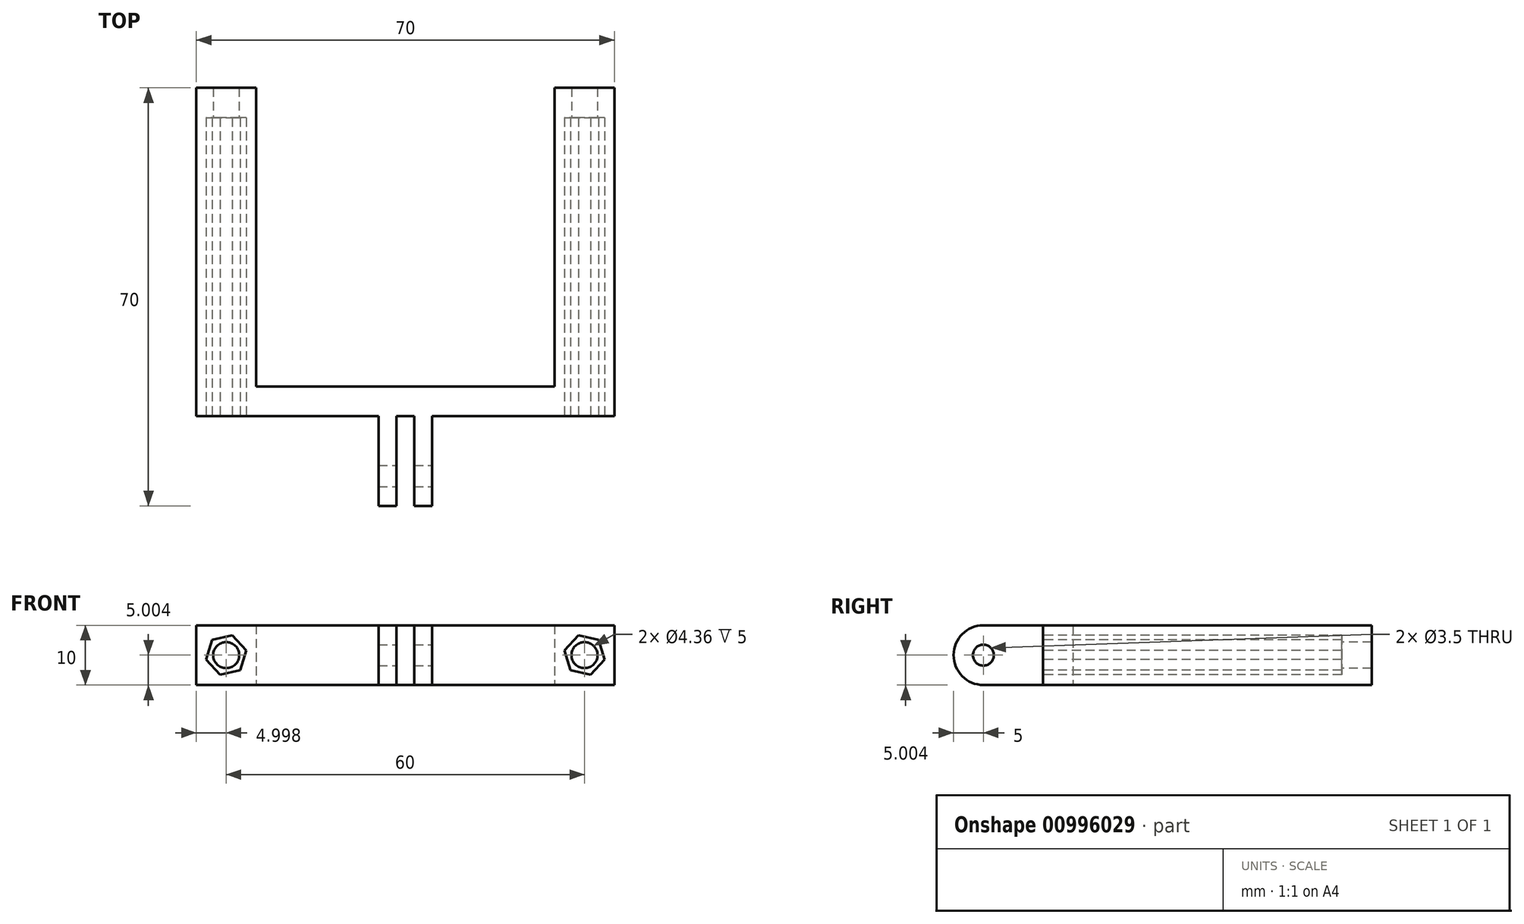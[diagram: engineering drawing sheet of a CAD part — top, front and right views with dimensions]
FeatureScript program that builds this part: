
annotation { "Feature Type Name" : "Feature", "Feature Type Description" : "" }
export const myFeature = defineFeature(function(context is Context, id is Id, definition is map)
    precondition{}
    {
        {
            var Q0;
            Q0=qCreatedBy(makeId("Front.planeOp"),FACE);
            var sketch = newSketch(context, id + "F0", { "sketchPlane" : qUnion([Q0])});
            skLineSegment(sketch, "E0.bottom", {"start": v(-29.53, -0.3) * mm, "end": v(-19.53, -0.3) * mm});
            skLineSegment(sketch, "E0.top", {"start": v(-29.53, -10.3) * mm, "end": v(-19.53, -10.3) * mm});
            skLineSegment(sketch, "E0.left", {"start": v(-29.53, -0.3) * mm, "end": v(-29.53, -10.3) * mm});
            skLineSegment(sketch, "E0.right", {"start": v(-19.53, -0.3) * mm, "end": v(-19.53, -10.3) * mm});
            skCircle(sketch, "E1", {"center": v(-24.53, -5.3) * mm, "radius": 2.18 * mm});
            skPoint(sketch, "E2", {"position": v(-24.53, -10.3) * mm});
            skPoint(sketch, "E3", {"position": v(-19.53, -5.3) * mm});
            skSolve(sketch);
        }
        {
            var Q0;
            Q0=makeQuery(id+"F0.imprint","IMPRINT",FACE,{"disambiguationData":[TD([[makeQuery(id+"F0.imprint","IMPRINT",EDGE,{"derivedFrom":sQuery(id+"F0.wireOp",EDGE,"rqn8Xpzs-wxr6-XT8o-bE4w-pqP2pNNWYZRO.bottom")}),-1.0]])]});
            var Q1;
            Q1=makeQuery(id+"F0.imprint","IMPRINT",FACE,{"disambiguationData":[TD([[makeQuery(id+"F0.imprint","IMPRINT",EDGE,{"derivedFrom":sQuery(id+"F0.wireOp",EDGE,"E0.bottom")}),-1.0]])]});
            extrude(context, id + "F1", {"entities" : qUnion([Q0, Q1]), "oppositeDirection" : true, "depth" : 50 * mm, "offsetDistance" : 25 * mm});
        }
        {
            var Q0;
            Q0=makeQuery(id+"F1.opExtrude","CAP_FACE",FACE,{"disambiguationData":[OSD([sQuery(id+"F0.wireOp",EDGE,"E0.bottom"),sQuery(id+"F0.wireOp",EDGE,"E0.top"),sQuery(id+"F0.wireOp",EDGE,"E0.left"),sQuery(id+"F0.wireOp",EDGE,"E0.right"),sQuery(id+"F0.wireOp",EDGE,"E1")])],"isStart":true});
            var sketch = newSketch(context, id + "F2", { "sketchPlane" : qUnion([Q0])});
            skLineSegment(sketch, "E4.0", {"start": v(30.47, -10.3) * mm, "end": v(40.47, -10.3) * mm});
            skLineSegment(sketch, "E5.bottom", {"start": v(-29.53, -0.3) * mm, "end": v(40.47, -0.3) * mm});
            skLineSegment(sketch, "E5.top", {"start": v(-29.53, -10.3) * mm, "end": v(40.47, -10.3) * mm});
            skLineSegment(sketch, "E5.left", {"start": v(-29.53, -0.3) * mm, "end": v(-29.53, -10.3) * mm});
            skLineSegment(sketch, "E5.right", {"start": v(40.47, -0.3) * mm, "end": v(40.47, -10.3) * mm});
            skCircle(sketch, "E6.cCircle", {"center": v(-24.53, -5.3) * mm, "radius": 3 * mm, "construction": true});
            skLineSegment(sketch, "E6.0", {"start": v(-21.15, -4.53) * mm, "end": v(-22.18, -7.84) * mm});
            skLineSegment(sketch, "E6.1", {"start": v(-22.18, -7.84) * mm, "end": v(-25.55, -8.62) * mm});
            skLineSegment(sketch, "E6.2", {"start": v(-25.55, -8.62) * mm, "end": v(-27.9, -6.08) * mm});
            skLineSegment(sketch, "E6.3", {"start": v(-27.9, -6.08) * mm, "end": v(-26.89, -2.77) * mm});
            skLineSegment(sketch, "E6.4", {"start": v(-26.89, -2.77) * mm, "end": v(-23.51, -2) * mm});
            skLineSegment(sketch, "E6.5", {"start": v(-23.51, -2) * mm, "end": v(-21.15, -4.53) * mm});
            skPoint(sketch, "E6.0.midPoint", {"position": v(-21.66, -6.19) * mm});
            skCircle(sketch, "E7.0", {"center": v(35.47, -5.3) * mm, "radius": 1.75 * mm});
            skCircle(sketch, "E8.cCircle", {"center": v(35.47, -5.3) * mm, "radius": 3 * mm, "construction": true});
            skLineSegment(sketch, "E8.0", {"start": v(38.92, -5.55) * mm, "end": v(36.99, -8.42) * mm});
            skLineSegment(sketch, "E8.1", {"start": v(36.99, -8.42) * mm, "end": v(33.53, -8.18) * mm});
            skLineSegment(sketch, "E8.2", {"start": v(33.53, -8.18) * mm, "end": v(32.01, -5.06) * mm});
            skLineSegment(sketch, "E8.3", {"start": v(32.01, -5.06) * mm, "end": v(33.95, -2.2) * mm});
            skLineSegment(sketch, "E8.4", {"start": v(33.95, -2.2) * mm, "end": v(37.4, -2.43) * mm});
            skLineSegment(sketch, "E8.5", {"start": v(37.4, -2.43) * mm, "end": v(38.92, -5.55) * mm});
            skPoint(sketch, "E8.0.midPoint", {"position": v(37.95, -6.98) * mm});
            skSolve(sketch);
        }
        {
            var Q0;
            Q0=makeQuery(id+"F2.imprint","IMPRINT",FACE,{"disambiguationData":[TD([[makeQuery(id+"F2.imprint","IMPRINT",EDGE,{"derivedFrom":sQuery(id+"F2.wireOp",EDGE,"E6.0")}),-1.0]])]});
            var Q1;
            Q1=makeQuery(id+"F2.imprint","IMPRINT",FACE,{"disambiguationData":[TD([[makeQuery(id+"F2.imprint","IMPRINT",EDGE,{"derivedFrom":sQuery(id+"F2.wireOp",EDGE,"E7.0")}),-1.0]])]});
            extrude(context, id + "F3", {"entities" : qUnion([Q0, Q1]), "operationType" : NewBodyOperationType.REMOVE, "oppositeDirection" : true, "depth" : 45 * mm, "offsetDistance" : 25 * mm});
        }
        {
            var Q0;
            Q0=makeQuery(id+"F1.opExtrude","CAP_FACE",FACE,{"disambiguationData":[OSD([sQuery(id+"F0.wireOp",EDGE,"E0.bottom"),sQuery(id+"F0.wireOp",EDGE,"E0.top"),sQuery(id+"F0.wireOp",EDGE,"E0.left"),sQuery(id+"F0.wireOp",EDGE,"E0.right"),sQuery(id+"F0.wireOp",EDGE,"E1")])],"isStart":true});
            var sketch = newSketch(context, id + "F4", { "sketchPlane" : qUnion([Q0])});
            skLineSegment(sketch, "E9.bottom", {"start": v(-29.53, -0.3) * mm, "end": v(5.47, -0.3) * mm});
            skLineSegment(sketch, "E9.top", {"start": v(-29.53, -10.3) * mm, "end": v(5.47, -10.3) * mm});
            skLineSegment(sketch, "E9.left", {"start": v(-29.53, -0.3) * mm, "end": v(-29.53, -10.3) * mm});
            skLineSegment(sketch, "E9.right", {"start": v(5.47, -0.3) * mm, "end": v(5.47, -10.3) * mm});
            skLineSegment(sketch, "E10.0", {"start": v(-25.55, -8.62) * mm, "end": v(-27.9, -6.08) * mm});
            skLineSegment(sketch, "E11.0", {"start": v(-27.9, -6.08) * mm, "end": v(-26.89, -2.77) * mm});
            skPoint(sketch, "E12.0", {"position": v(-26.89, -2.77) * mm});
            skLineSegment(sketch, "E13.0", {"start": v(-26.89, -2.77) * mm, "end": v(-23.51, -2) * mm});
            skPoint(sketch, "E14.0", {"position": v(-22.33, -3.27) * mm});
            skLineSegment(sketch, "E15.0", {"start": v(-23.51, -2) * mm, "end": v(-21.15, -4.53) * mm});
            skLineSegment(sketch, "E16.0", {"start": v(-21.15, -4.53) * mm, "end": v(-22.18, -7.84) * mm});
            skLineSegment(sketch, "E17.0", {"start": v(-22.18, -7.84) * mm, "end": v(-25.55, -8.62) * mm});
            skSolve(sketch);
        }
        {
            var Q0;
            Q0 = qSketchRegion(id + "F4", true);
            extrude(context, id + "F5", {"entities" : qUnion([Q0]), "operationType" : NewBodyOperationType.ADD, "depth" : 5 * mm, "offsetDistance" : 25 * mm});
        }
        {
            var Q0;
            Q0=makeQuery(id+"F1.opExtrude","SWEPT_BODY",BODY,{"disambiguationData":[OSD([sQuery(id+"F0.wireOp",EDGE,"E0.bottom"),sQuery(id+"F0.wireOp",EDGE,"E0.top"),sQuery(id+"F0.wireOp",EDGE,"E0.left"),sQuery(id+"F0.wireOp",EDGE,"E0.right"),sQuery(id+"F0.wireOp",EDGE,"E1")])]});
            var Q1;
            Q1=makeQuery(id+"F5.opExtrude","SWEPT_FACE",FACE,{"disambiguationData":[OSD([sQuery(id+"F4.wireOp",EDGE,"E9.right")])]});
            mirror(context, id + "F6", {"operationType" : NewBodyOperationType.ADD, "entities" : qUnion([Q0]), "mirrorPlane" : qUnion([Q1])});
        }
        {
            var Q0;
            {var subQ0=makeQuery(id+"F5.opExtrude","CAP_FACE",FACE,{"disambiguationData":[OSD([sQuery(id+"F4.wireOp",EDGE,"E9.bottom"),sQuery(id+"F4.wireOp",EDGE,"E9.top"),sQuery(id+"F4.wireOp",EDGE,"E9.left"),sQuery(id+"F4.wireOp",EDGE,"E9.right"),sQuery(id+"F4.wireOp",EDGE,"E10.0"),sQuery(id+"F4.wireOp",EDGE,"E11.0"),sQuery(id+"F4.wireOp",EDGE,"E13.0"),sQuery(id+"F4.wireOp",EDGE,"E15.0"),sQuery(id+"F4.wireOp",EDGE,"E16.0"),sQuery(id+"F4.wireOp",EDGE,"E17.0")])],"isStart":false});Q0=makeQuery(id+"F6.boolean.opBoolean","MERGE",FACE,{"derivedFrom":[subQ0,makeQuery(id+"F6.opPattern","COPY",FACE,{"derivedFrom":subQ0,"instanceName":"1"})]});}
            var sketch = newSketch(context, id + "F7", { "sketchPlane" : qUnion([Q0])});
            skLineSegment(sketch, "E18.0", {"start": v(-29.53, -0.3) * mm, "end": v(40.47, -0.3) * mm});
            skLineSegment(sketch, "E19.0", {"start": v(-29.53, -10.3) * mm, "end": v(40.47, -10.3) * mm});
            skPoint(sketch, "E20", {"position": v(5.47, -0.3) * mm});
            skPoint(sketch, "E21", {"position": v(5.47, -10.3) * mm});
            skLineSegment(sketch, "E22", {"start": v(5.47, -0.3) * mm, "end": v(5.47, -10.3) * mm, "construction": true});
            skLineSegment(sketch, "E23.bottom", {"start": v(3.97, -0.3) * mm, "end": v(0.97, -0.3) * mm});
            skLineSegment(sketch, "E23.top", {"start": v(3.97, -10.3) * mm, "end": v(0.97, -10.3) * mm});
            skLineSegment(sketch, "E23.left", {"start": v(3.97, -0.3) * mm, "end": v(3.97, -10.3) * mm});
            skLineSegment(sketch, "E23.right", {"start": v(0.97, -0.3) * mm, "end": v(0.97, -10.3) * mm});
            skLineSegment(sketch, "E24.bottom", {"start": v(6.97, -0.3) * mm, "end": v(9.97, -0.3) * mm});
            skLineSegment(sketch, "E24.top", {"start": v(6.97, -10.3) * mm, "end": v(9.97, -10.3) * mm});
            skLineSegment(sketch, "E24.left", {"start": v(6.97, -0.3) * mm, "end": v(6.97, -10.3) * mm});
            skLineSegment(sketch, "E24.right", {"start": v(9.97, -0.3) * mm, "end": v(9.97, -10.3) * mm});
            skSolve(sketch);
        }
        {
            var Q0;
            {var subQ0=sQuery(id+"F7.wireOp",EDGE,"E24.left");Q0=makeQuery(id+"F7.imprint","IMPRINT",FACE,{"disambiguationData":[TD([[makeQuery(id+"F7.imprint","IMPRINT",EDGE,{"derivedFrom":subQ0}),1.0]])]});}
            var Q1;
            {var subQ0=sQuery(id+"F7.wireOp",EDGE,"E23.left");Q1=makeQuery(id+"F7.imprint","IMPRINT",FACE,{"disambiguationData":[TD([[makeQuery(id+"F7.imprint","IMPRINT",EDGE,{"derivedFrom":subQ0}),-1.0]])]});}
            extrude(context, id + "F8", {"entities" : qUnion([Q0, Q1]), "operationType" : NewBodyOperationType.ADD, "depth" : 15 * mm, "offsetDistance" : 25 * mm});
        }
        {
            var Q0;
            Q0=makeQuery(id+"F8.opExtrude","SWEPT_FACE",FACE,{"disambiguationData":[OSD([sQuery(id+"F7.wireOp",EDGE,"E24.right")])]});
            var sketch = newSketch(context, id + "F9", { "sketchPlane" : qUnion([Q0])});
            skArc(sketch, "E25", {"start": v(-15, -0.3) * mm, "mid": v(-20, -5.3) * mm, "end": v(-15, -10.3) * mm});
            skLineSegment(sketch, "E26", {"start": v(-20, -0.3) * mm, "end": v(-15, -0.3) * mm});
            skLineSegment(sketch, "E27", {"start": v(-20, -10.3) * mm, "end": v(-15, -10.3) * mm});
            skLineSegment(sketch, "E28", {"start": v(-20, -0.3) * mm, "end": v(-20, -10.3) * mm});
            skCircle(sketch, "E29", {"center": v(-15, -5.3) * mm, "radius": 1.75 * mm});
            skSolve(sketch);
        }
        {
            var Q0;
            {var subQ0=sQuery(id+"F9.wireOp",EDGE,"E26");Q0=makeQuery(id+"F9.imprint","IMPRINT",FACE,{"disambiguationData":[TD([[makeQuery(id+"F9.imprint","IMPRINT",EDGE,{"derivedFrom":subQ0}),-1.0]])]});}
            var Q1;
            Q1=makeQuery(id+"F9.imprint","IMPRINT",FACE,{"disambiguationData":[TD([[makeQuery(id+"F9.imprint","IMPRINT",EDGE,{"derivedFrom":sQuery(id+"F9.wireOp",EDGE,"E29")}),1.0]])]});
            var Q2;
            {var subQ0=sQuery(id+"F9.wireOp",EDGE,"E27");Q2=makeQuery(id+"F9.imprint","IMPRINT",FACE,{"disambiguationData":[TD([[makeQuery(id+"F9.imprint","IMPRINT",EDGE,{"derivedFrom":subQ0}),1.0]])]});}
            extrude(context, id + "F10", {"entities" : qUnion([Q0, Q1, Q2]), "operationType" : NewBodyOperationType.REMOVE, "endBound" : BoundingType.THROUGH_ALL, "oppositeDirection" : true, "depth" : 25 * mm, "offsetDistance" : 25 * mm});
        }
    });
